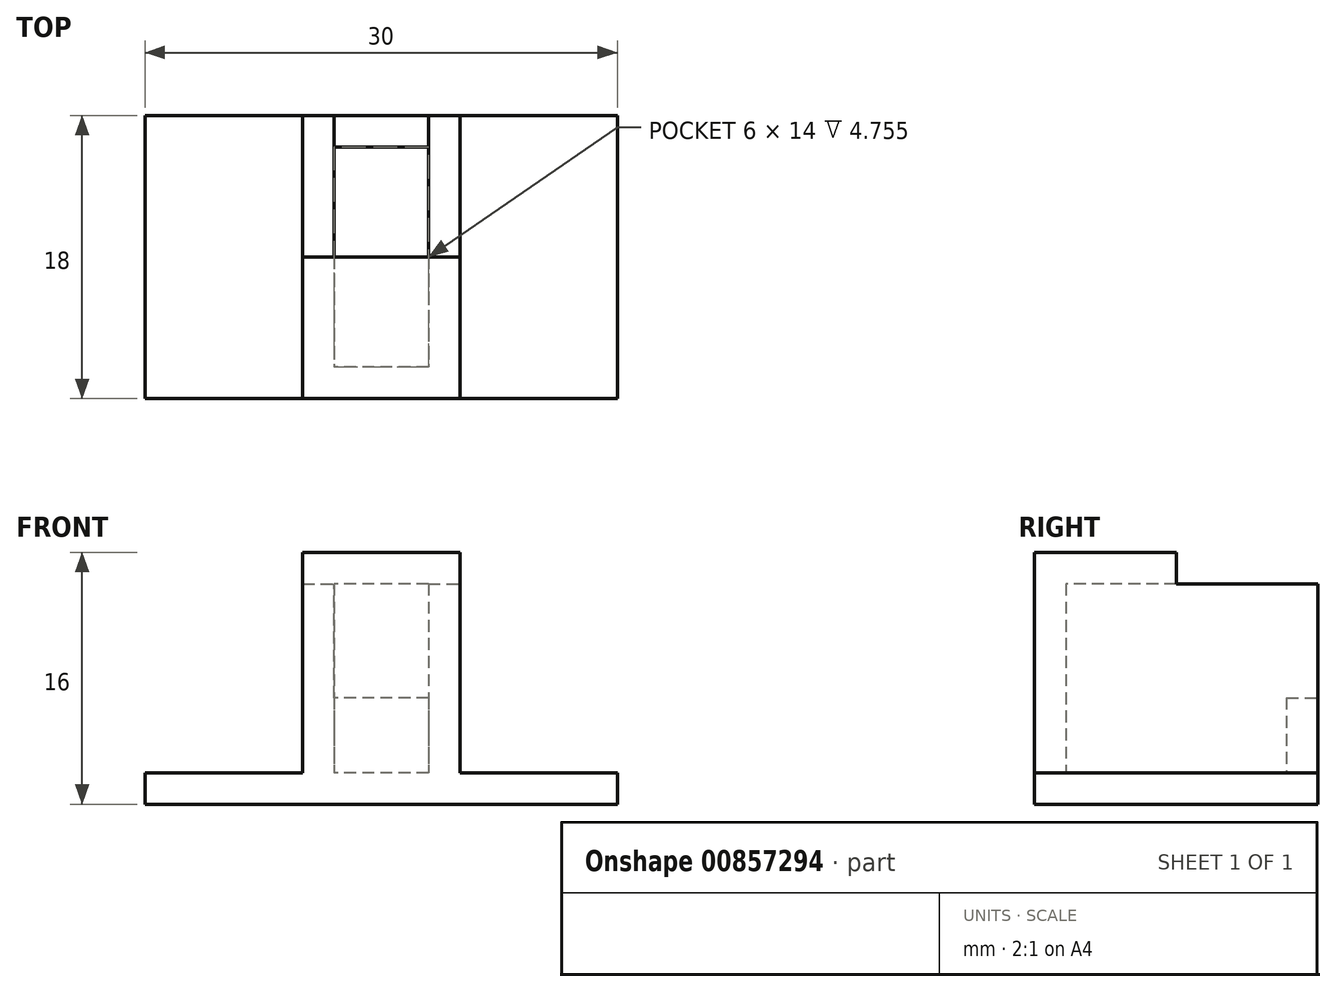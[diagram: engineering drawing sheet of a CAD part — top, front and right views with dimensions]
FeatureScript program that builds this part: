
annotation { "Feature Type Name" : "Feature", "Feature Type Description" : "" }
export const myFeature = defineFeature(function(context is Context, id is Id, definition is map)
    precondition{}
    {
        {
            var Q0;
            Q0=qCreatedBy(makeId("Top.planeOp"),FACE);
            var sketch = newSketch(context, id + "F0", { "sketchPlane" : qUnion([Q0])});
            skLineSegment(sketch, "E0.bottom", {"start": v(15, 9) * mm, "end": v(-15, 9) * mm});
            skLineSegment(sketch, "E0.top", {"start": v(15, -9) * mm, "end": v(-15, -9) * mm});
            skLineSegment(sketch, "E0.left", {"start": v(15, 9) * mm, "end": v(15, -9) * mm});
            skLineSegment(sketch, "E0.right", {"start": v(-15, 9) * mm, "end": v(-15, -9) * mm});
            skPoint(sketch, "E0.middle", {"position": v(0, 0) * mm});
            skSolve(sketch);
        }
        {
            var Q0;
            Q0 = qSketchRegion(id + "F0", true);
            extrude(context, id + "F1", {"entities" : qUnion([Q0]), "depth" : 2 * mm, "offsetDistance" : 25 * mm});
        }
        {
            var Q0;
            Q0=makeQuery(id+"F1.opExtrude","CAP_FACE",FACE,{"disambiguationData":[OSD([sQuery(id+"F0.wireOp",EDGE,"E0.bottom"),sQuery(id+"F0.wireOp",EDGE,"E0.top"),sQuery(id+"F0.wireOp",EDGE,"E0.left"),sQuery(id+"F0.wireOp",EDGE,"E0.right")])],"isStart":false});
            cPlane(context, id + "F2", {"entities" : qUnion([Q0]), "cplaneType" : CPlaneType.OFFSET, "offset" : 0 * mm, "width" : 150 * mm, "height" : 150 * mm});
        }
        {
            var Q0;
            Q0=qCreatedBy(id+"F2.planeOp",FACE);
            var sketch = newSketch(context, id + "F3", { "sketchPlane" : qUnion([Q0])});
            skLineSegment(sketch, "E1.bottom", {"start": v(5, 9) * mm, "end": v(-5, 9) * mm});
            skLineSegment(sketch, "E1.top", {"start": v(5, -9) * mm, "end": v(-5, -9) * mm});
            skLineSegment(sketch, "E1.left", {"start": v(5, 9) * mm, "end": v(5, -9) * mm});
            skLineSegment(sketch, "E1.right", {"start": v(-5, 9) * mm, "end": v(-5, -9) * mm});
            skPoint(sketch, "E1.middle", {"position": v(0, 0) * mm});
            skLineSegment(sketch, "E2.0", {"start": v(3, 7) * mm, "end": v(3, -7) * mm});
            skLineSegment(sketch, "E2.1", {"start": v(3, 7) * mm, "end": v(-3, 7) * mm});
            skLineSegment(sketch, "E2.2", {"start": v(-3, 7) * mm, "end": v(-3, -7) * mm});
            skLineSegment(sketch, "E2.3", {"start": v(3, -7) * mm, "end": v(-3, -7) * mm});
            skSolve(sketch);
        }
        {
            var Q0;
            Q0 = qSketchRegion(id + "F3", true);
            extrude(context, id + "F4", {"entities" : qUnion([Q0]), "operationType" : NewBodyOperationType.ADD, "depth" : 12 * mm, "offsetDistance" : 25 * mm});
        }
        {
            var Q0;
            Q0=makeQuery(id+"F4.boolean.opBoolean","MERGE",FACE,{"derivedFrom":[makeQuery(id+"F1.opExtrude","SWEPT_FACE",FACE,{"disambiguationData":[OSD([sQuery(id+"F0.wireOp",EDGE,"E0.bottom")])]}),makeQuery(id+"F4.opExtrude","SWEPT_FACE",FACE,{"disambiguationData":[OSD([sQuery(id+"F3.wireOp",EDGE,"E1.bottom")])]})]});
            cPlane(context, id + "F5", {"entities" : qUnion([Q0]), "cplaneType" : CPlaneType.OFFSET, "offset" : 0 * mm, "width" : 150 * mm, "height" : 150 * mm});
        }
        {
            var Q0;
            Q0=qCreatedBy(id+"F5.planeOp",FACE);
            var sketch = newSketch(context, id + "F6", { "sketchPlane" : qUnion([Q0])});
            skPoint(sketch, "E3.0", {"position": v(-3, 14) * mm});
            skLineSegment(sketch, "E4.0", {"start": v(5, 14) * mm, "end": v(5, 2) * mm});
            skLineSegment(sketch, "E5.0", {"start": v(-5, 14) * mm, "end": v(-5, 2) * mm});
            skPoint(sketch, "E6.0", {"position": v(3, 14) * mm});
            skLineSegment(sketch, "E7.0.0", {"start": v(-15, 0) * mm, "end": v(15, 0) * mm});
            skLineSegment(sketch, "E7.0.1", {"start": v(15, 0) * mm, "end": v(15, 2) * mm});
            skLineSegment(sketch, "E7.0.2", {"start": v(15, 2) * mm, "end": v(5, 2) * mm});
            skLineSegment(sketch, "E7.0.3", {"start": v(5, 2) * mm, "end": v(5, 14) * mm});
            skLineSegment(sketch, "E7.0.4", {"start": v(5, 14) * mm, "end": v(-5, 14) * mm});
            skLineSegment(sketch, "E7.0.6", {"start": v(-5, 2) * mm, "end": v(-15, 2) * mm});
            skLineSegment(sketch, "E7.0.7", {"start": v(-15, 2) * mm, "end": v(-15, 0) * mm});
            skLineSegment(sketch, "E8", {"start": v(-3, 14) * mm, "end": v(-3, 6.75) * mm});
            skLineSegment(sketch, "E9", {"start": v(-3, 6.75) * mm, "end": v(3, 6.75) * mm});
            skLineSegment(sketch, "E10", {"start": v(3, 6.75) * mm, "end": v(3, 14) * mm});
            skSolve(sketch);
        }
        {
            var Q0;
            {var subQ0=sQuery(id+"F6.wireOp",EDGE,"E8");Q0=makeQuery(id+"F6.imprint","IMPRINT",FACE,{"disambiguationData":[TD([[makeQuery(id+"F6.imprint","IMPRINT",EDGE,{"derivedFrom":subQ0}),1.0]])]});}
            extrude(context, id + "F7", {"entities" : qUnion([Q0]), "operationType" : NewBodyOperationType.REMOVE, "oppositeDirection" : true, "depth" : 4 * mm, "offsetDistance" : 25 * mm});
        }
        {
            var Q0;
            Q0=makeQuery(id+"F4.opExtrude","CAP_FACE",FACE,{"disambiguationData":[OSD([sQuery(id+"F3.wireOp",EDGE,"E1.bottom"),sQuery(id+"F3.wireOp",EDGE,"E1.top"),sQuery(id+"F3.wireOp",EDGE,"E1.left"),sQuery(id+"F3.wireOp",EDGE,"E1.right"),sQuery(id+"F3.wireOp",EDGE,"E2.0"),sQuery(id+"F3.wireOp",EDGE,"E2.1"),sQuery(id+"F3.wireOp",EDGE,"E2.2"),sQuery(id+"F3.wireOp",EDGE,"E2.3")])],"isStart":false});
            cPlane(context, id + "F8", {"entities" : qUnion([Q0]), "cplaneType" : CPlaneType.OFFSET, "offset" : 0 * mm, "width" : 150 * mm, "height" : 150 * mm});
        }
        {
            var Q0;
            Q0=qCreatedBy(id+"F8.planeOp",FACE);
            var sketch = newSketch(context, id + "F9", { "sketchPlane" : qUnion([Q0])});
            skLineSegment(sketch, "E11.0", {"start": v(-5, 0) * mm, "end": v(-5, -9) * mm});
            skPoint(sketch, "E12.0", {"position": v(0, -9) * mm});
            skLineSegment(sketch, "E13.0", {"start": v(5, 0) * mm, "end": v(5, -9) * mm});
            skLineSegment(sketch, "E14", {"start": v(-5, 0) * mm, "end": v(5, 0) * mm});
            skPoint(sketch, "E15.orphan", {"position": v(-5, 9) * mm});
            skPoint(sketch, "E16.orphan", {"position": v(5, 9) * mm});
            skLineSegment(sketch, "E17", {"start": v(-5, -9) * mm, "end": v(5, -9) * mm});
            skSolve(sketch);
        }
        {
            var Q0;
            Q0 = qSketchRegion(id + "F9", true);
            extrude(context, id + "F10", {"entities" : qUnion([Q0]), "operationType" : NewBodyOperationType.ADD, "depth" : 2 * mm, "offsetDistance" : 25 * mm});
        }
    });
